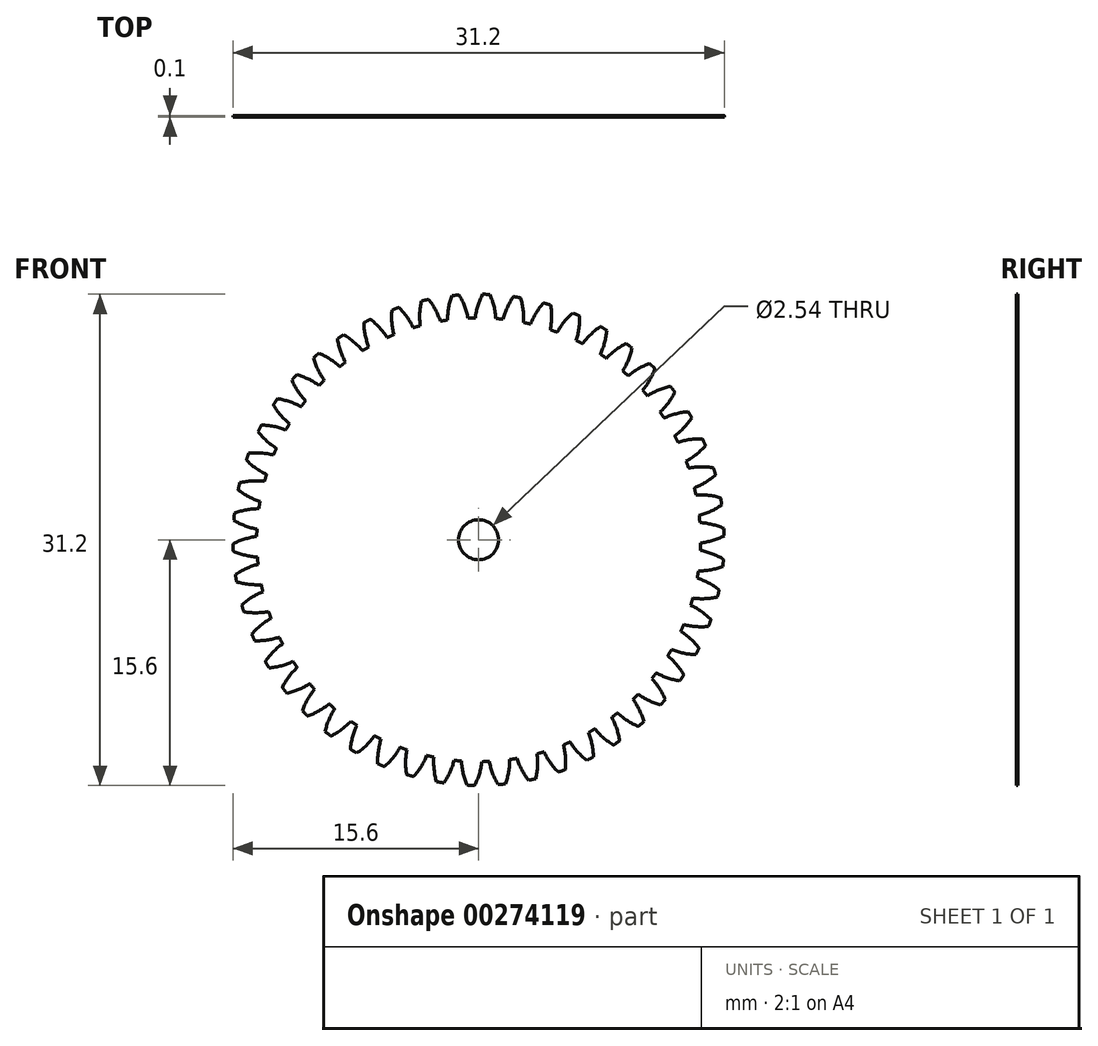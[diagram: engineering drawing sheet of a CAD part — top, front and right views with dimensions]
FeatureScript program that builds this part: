
annotation { "Feature Type Name" : "Feature", "Feature Type Description" : "" }
export const myFeature = defineFeature(function(context is Context, id is Id, definition is map)
    precondition{}
    {
        {
            assignVariable(context, id + "F0", {"name" : "teeth", "anyValue" : 50});
        }
        {
            assignVariable(context, id + "F1", {"name" : "thickness", "anyValue" : 0.1});
        }
        {
            var Q0;
            Q0=qCreatedBy(makeId("Front.planeOp"),FACE);
            var sketch = newSketch(context, id + "F2", { "sketchPlane" : qUnion([Q0])});
            skCircle(sketch, "E0", {"center": v(0, 0) * mm, "radius": 15 * mm, "construction": true});
            skCircle(sketch, "E1", {"center": v(0, 0) * mm, "radius": 15.6 * mm, "construction": true});
            skCircle(sketch, "E2", {"center": v(0, 0) * mm, "radius": 14.1 * mm});
            skCircle(sketch, "E3", {"center": v(30, 0) * mm, "radius": 14.1 * mm, "construction": true});
            skLineSegment(sketch, "E4", {"start": v(13.25, 4.82) * mm, "end": v(15, 0) * mm, "construction": true});
            skLineSegment(sketch, "E5", {"start": v(0, 0) * mm, "end": v(15, 0) * mm, "construction": true});
            skLineSegment(sketch, "E6", {"start": v(15, 0) * mm, "end": v(15, 28.46) * mm, "construction": true});
            skLineSegment(sketch, "E7", {"start": v(15, 0) * mm, "end": v(16.75, -4.82) * mm, "construction": true});
            skLineSegment(sketch, "E8", {"start": v(15, 0) * mm, "end": v(30, 0) * mm, "construction": true});
            skLineSegment(sketch, "E9", {"start": v(13.25, 4.82) * mm, "end": v(0, 0) * mm, "construction": true});
            skArc(sketch, "E10", {"start": v(13.25, 4.82) * mm, "mid": v(13.9, 2.34) * mm, "end": v(14.1, -0.21) * mm, "construction": true});
            skArc(sketch, "E11", {"start": v(14.1, -0.21) * mm, "mid": v(13.75, 3.1) * mm, "end": v(12.63, 6.25) * mm, "construction": true});
            skLineSegment(sketch, "E12", {"start": v(12.63, 6.25) * mm, "end": v(0, 0) * mm, "construction": true});
            skLineSegment(sketch, "E13", {"start": v(12.63, 6.25) * mm, "end": v(15.6, 0.26) * mm, "construction": true});
            skLineSegment(sketch, "E14", {"start": v(14.1, -0.21) * mm, "end": v(0, 0) * mm, "construction": true});
            skArc(sketch, "E15", {"start": v(14.1, -0.21) * mm, "mid": v(14.87, -0.04) * mm, "end": v(15.6, 0.26) * mm});
            skLineSegment(sketch, "E16", {"start": v(0, 0) * mm, "end": v(15.6, 0.5) * mm, "construction": true});
            skArc(sketch, "E17.MirrorCS", {"start": v(14.05, 1.1) * mm, "mid": v(14.83, 0.98) * mm, "end": v(15.58, 0.72) * mm});
            skPoint(sketch, "E18", {"position": v(14.97, 0.94) * mm});
            skArc(sketch, "E19", {"start": v(15.6, 0.26) * mm, "mid": v(15.6, 0.5) * mm, "end": v(15.58, 0.72) * mm});
            skPoint(sketch, "E20", {"position": v(14.09, 0.44) * mm});
            skArc(sketch, "E21", {"start": v(14.1, -0.21) * mm, "mid": v(14.09, 0.44) * mm, "end": v(14.05, 1.1) * mm});
            skCircle(sketch, "E22", {"center": v(0, 0) * mm, "radius": 1.27 * mm});
            skSolve(sketch);
        }
        {
            var Q0;
            {var subQ0=sQuery(id+"F2.wireOp",EDGE,"E2");var subQ1=makeQuery(id+"F2.imprint","INTERSECT",VERTEX,{"derivedFrom":[subQ0,sQuery(id+"F2.wireOp",EDGE,"E15")]});Q0=makeQuery(id+"F2.imprint","IMPRINT",FACE,{"disambiguationData":[TD([[makeQuery(id+"F2.imprint","IMPRINT",EDGE,{"disambiguationData":[TD([[subQ1,1.0]])],"derivedFrom":subQ0}),1.0]])]});}
            extrude(context, id + "F3", {"entities" : qUnion([Q0]), "depth" : (getVariable(context, 'thickness')) * mm});
        }
        {
            var Q0;
            {var subQ0=sQuery(id+"F2.wireOp",EDGE,"E15");Q0=makeQuery(id+"F2.imprint","IMPRINT",FACE,{"disambiguationData":[TD([[makeQuery(id+"F2.imprint","IMPRINT",EDGE,{"derivedFrom":subQ0}),1.0]])]});}
            extrude(context, id + "F4", {"entities" : qUnion([Q0]), "depth" : (getVariable(context, 'thickness')) * mm});
        }
        {
            var Q0;
            Q0=qCreatedBy(makeId("Right.planeOp"),FACE);
            var sketch = newSketch(context, id + "F5", { "sketchPlane" : qUnion([Q0])});
            skLineSegment(sketch, "E23", {"start": v(0, 0) * mm, "end": v(12.3, 0) * mm});
            skSolve(sketch);
        }
        {
            var Q0;
            Q0=makeQuery(id+"F4.opExtrude","SWEPT_BODY",BODY,{"disambiguationData":[OSD([sQuery(id+"F2.wireOp",EDGE,"E2"),sQuery(id+"F2.wireOp",EDGE,"E15"),sQuery(id+"F2.wireOp",EDGE,"E17.MirrorCS"),sQuery(id+"F2.wireOp",EDGE,"E19")])]});
            var Q1;
            Q1=sQuery(id+"F5.wireOp",EDGE,"E23");
            circularPattern(context, id + "F6", {"operationType" : NewBodyOperationType.ADD, "entities" : qUnion([Q0]), "axis" : qUnion([Q1]), "angle" : (360 / getVariable(context, 'teeth')) * degree, "instanceCount" : getVariable(context, 'teeth')});
        }
    });
